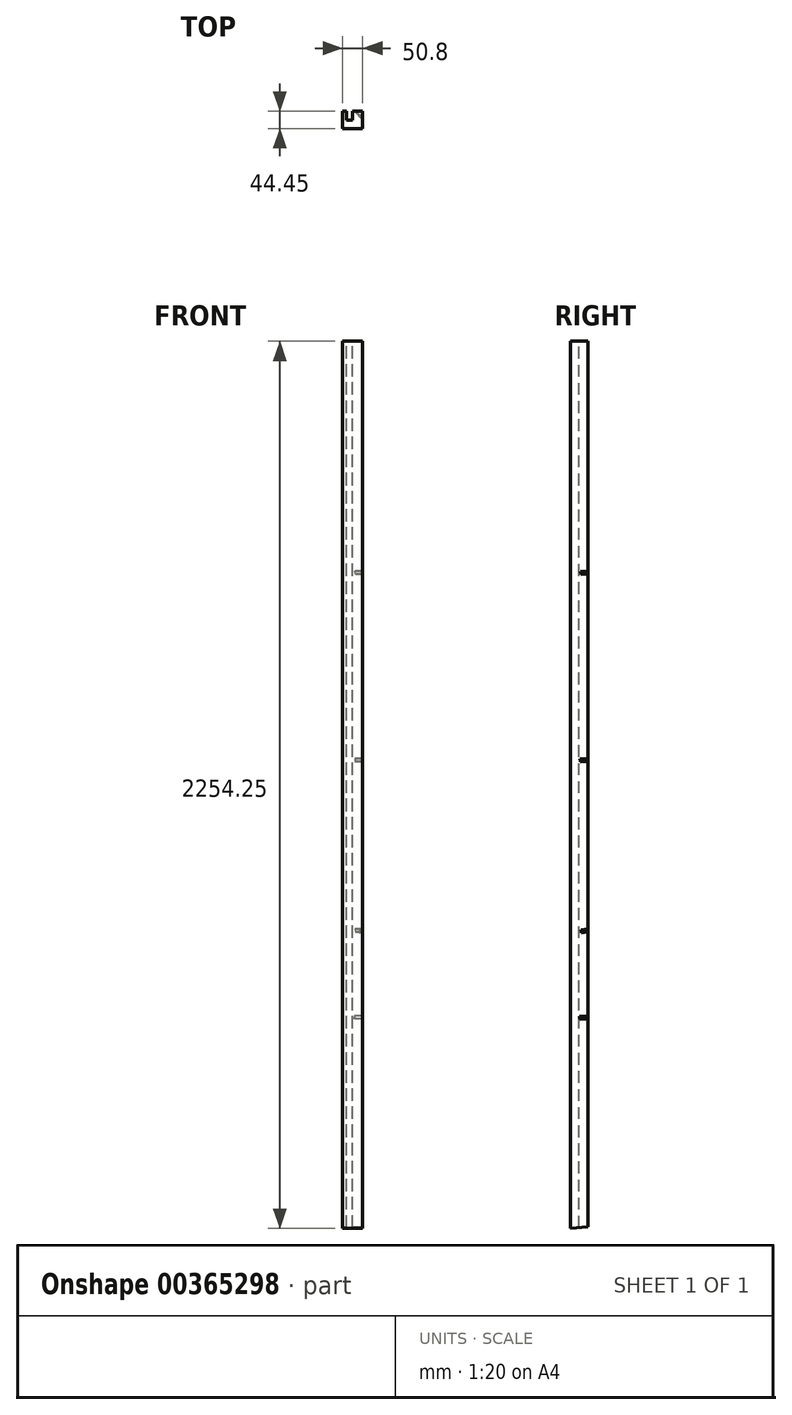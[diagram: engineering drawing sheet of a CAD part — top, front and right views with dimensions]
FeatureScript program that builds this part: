
annotation { "Feature Type Name" : "Feature", "Feature Type Description" : "" }
export const myFeature = defineFeature(function(context is Context, id is Id, definition is map)
    precondition{}
    {
        {
            var Q0;
            Q0=qCreatedBy(makeId("Top.planeOp"),FACE);
            var sketch = newSketch(context, id + "F0", { "sketchPlane" : qUnion([Q0])});
            skLineSegment(sketch, "E0.bottom", {"start": v(0, 0) * mm, "end": v(50.8, 0) * mm});
            skLineSegment(sketch, "E0.top", {"start": v(0, 44.45) * mm, "end": v(50.8, 44.45) * mm});
            skLineSegment(sketch, "E0.left", {"start": v(0, 0) * mm, "end": v(0, 44.45) * mm});
            skLineSegment(sketch, "E0.right", {"start": v(50.8, 0) * mm, "end": v(50.8, 44.45) * mm});
            skSolve(sketch);
        }
        {
            var Q0;
            Q0=makeQuery(id+"F0.imprint","IMPRINT",FACE,{"disambiguationData":[TD([[makeQuery(id+"F0.imprint","IMPRINT",EDGE,{"derivedFrom":sQuery(id+"F0.wireOp",EDGE,"E0.bottom")}),1.0]])]});
            extrude(context, id + "F1", {"entities" : qUnion([Q0]), "depth" : 2254.25 * mm});
        }
        {
            var Q0;
            Q0=makeQuery(id+"F1.opExtrude","CAP_FACE",FACE,{"disambiguationData":[OSD([sQuery(id+"F0.wireOp",EDGE,"E0.bottom"),sQuery(id+"F0.wireOp",EDGE,"E0.top"),sQuery(id+"F0.wireOp",EDGE,"E0.left"),sQuery(id+"F0.wireOp",EDGE,"E0.right")])],"isStart":false});
            var sketch = newSketch(context, id + "F2", { "sketchPlane" : qUnion([Q0])});
            skLineSegment(sketch, "E1.bottom", {"start": v(9.53, 44.45) * mm, "end": v(25.4, 44.45) * mm});
            skLineSegment(sketch, "E1.top", {"start": v(9.53, 22.23) * mm, "end": v(25.4, 22.23) * mm});
            skLineSegment(sketch, "E1.left", {"start": v(9.53, 44.45) * mm, "end": v(9.53, 22.23) * mm});
            skLineSegment(sketch, "E1.right", {"start": v(25.4, 44.45) * mm, "end": v(25.4, 22.23) * mm});
            skSolve(sketch);
        }
        {
            var Q0;
            Q0=makeQuery(id+"F2.imprint","IMPRINT",FACE,{"disambiguationData":[TD([[makeQuery(id+"F2.imprint","IMPRINT",EDGE,{"derivedFrom":sQuery(id+"F2.wireOp",EDGE,"E1.bottom")}),-1.0]])]});
            extrude(context, id + "F3", {"entities" : qUnion([Q0]), "operationType" : NewBodyOperationType.REMOVE, "oppositeDirection" : true, "depth" : 2260.6 * mm});
        }
        {
            var Q0;
            Q0=makeQuery(id+"F1.opExtrude","SWEPT_FACE",FACE,{"disambiguationData":[OSD([sQuery(id+"F0.wireOp",EDGE,"E0.right")])]});
            var sketch = newSketch(context, id + "F4", { "sketchPlane" : qUnion([Q0])});
            skLineSegment(sketch, "E2", {"start": v(0, 0) * mm, "end": v(44.45, 3.89) * mm});
            skLineSegment(sketch, "E3", {"start": v(44.45, 3.89) * mm, "end": v(44.45, 0) * mm});
            skLineSegment(sketch, "E4", {"start": v(44.45, 0) * mm, "end": v(0, 0) * mm});
            skSolve(sketch);
        }
        {
            var Q0;
            Q0=makeQuery(id+"F4.imprint","IMPRINT",FACE,{"disambiguationData":[TD([[makeQuery(id+"F4.imprint","IMPRINT",EDGE,{"derivedFrom":sQuery(id+"F4.wireOp",EDGE,"E2")}),-1.0]])]});
            extrude(context, id + "F5", {"entities" : qUnion([Q0]), "operationType" : NewBodyOperationType.REMOVE, "oppositeDirection" : true, "depth" : 76.2 * mm});
        }
        {
            var Q0;
            Q0=makeQuery(id+"F5.boolean.opBoolean","COPY",FACE,{"derivedFrom":makeQuery(id+"F5.opExtrude","SWEPT_FACE",FACE,{"disambiguationData":[OSD([sQuery(id+"F4.wireOp",EDGE,"E2")])]})});
            cPlane(context, id + "F6", {"entities" : qUnion([Q0]), "cplaneType" : CPlaneType.OFFSET, "offset" : 527.05 * mm, "oppositeDirection" : true, "width" : 152.4 * mm, "height" : 152.4 * mm});
        }
        {
            var Q0;
            Q0=makeQuery(id+"F5.boolean.opBoolean","COPY",FACE,{"derivedFrom":makeQuery(id+"F5.opExtrude","SWEPT_FACE",FACE,{"disambiguationData":[OSD([sQuery(id+"F4.wireOp",EDGE,"E2")])]})});
            cPlane(context, id + "F7", {"entities" : qUnion([Q0]), "cplaneType" : CPlaneType.OFFSET, "offset" : 746.12 * mm, "oppositeDirection" : true, "width" : 152.4 * mm, "height" : 152.4 * mm});
        }
        {
            var Q0;
            Q0=makeQuery(id+"F5.boolean.opBoolean","COPY",FACE,{"derivedFrom":makeQuery(id+"F5.opExtrude","SWEPT_FACE",FACE,{"disambiguationData":[OSD([sQuery(id+"F4.wireOp",EDGE,"E2")])]})});
            cPlane(context, id + "F8", {"entities" : qUnion([Q0]), "cplaneType" : CPlaneType.OFFSET, "offset" : 1177.92 * mm, "oppositeDirection" : true, "width" : 152.4 * mm, "height" : 152.4 * mm});
        }
        {
            var Q0;
            Q0=makeQuery(id+"F5.boolean.opBoolean","COPY",FACE,{"derivedFrom":makeQuery(id+"F5.opExtrude","SWEPT_FACE",FACE,{"disambiguationData":[OSD([sQuery(id+"F4.wireOp",EDGE,"E2")])]})});
            cPlane(context, id + "F9", {"entities" : qUnion([Q0]), "cplaneType" : CPlaneType.OFFSET, "offset" : 1660.52 * mm, "oppositeDirection" : true, "width" : 152.4 * mm, "height" : 152.4 * mm});
        }
        {
            var Q0;
            Q0=qCreatedBy(id+"F6.planeOp",FACE);
            var sketch = newSketch(context, id + "F10", { "sketchPlane" : qUnion([Q0])});
            skLineSegment(sketch, "E5", {"start": v(52.64, -68.17) * mm, "end": v(29.97, -90.85) * mm});
            skLineSegment(sketch, "E6", {"start": v(29.97, -90.85) * mm, "end": v(45.66, -106.54) * mm});
            skLineSegment(sketch, "E7", {"start": v(45.66, -106.54) * mm, "end": v(68.34, -83.87) * mm});
            skLineSegment(sketch, "E8", {"start": v(68.34, -83.87) * mm, "end": v(52.64, -68.17) * mm});
            skSolve(sketch);
        }
        {
            var Q0;
            Q0=makeQuery(id+"F10.imprint","IMPRINT",FACE,{"disambiguationData":[TD([[makeQuery(id+"F10.imprint","IMPRINT",EDGE,{"derivedFrom":sQuery(id+"F10.wireOp",EDGE,"E5")}),1.0]])]});
            extrude(context, id + "F11", {"entities" : qUnion([Q0]), "operationType" : NewBodyOperationType.REMOVE, "oppositeDirection" : true, "depth" : 7.62 * mm});
        }
        {
            var Q0;
            Q0=qCreatedBy(id+"F7.planeOp",FACE);
            var sketch = newSketch(context, id + "F12", { "sketchPlane" : qUnion([Q0])});
            skLineSegment(sketch, "E9", {"start": v(30.08, -111.42) * mm, "end": v(50.8, -93.16) * mm});
            skLineSegment(sketch, "E10", {"start": v(50.8, -93.16) * mm, "end": v(68.8, -113.6) * mm});
            skLineSegment(sketch, "E11", {"start": v(68.8, -113.6) * mm, "end": v(48.08, -131.84) * mm});
            skLineSegment(sketch, "E12", {"start": v(48.08, -131.84) * mm, "end": v(30.08, -111.42) * mm});
            skSolve(sketch);
        }
        {
            var Q0;
            Q0=makeQuery(id+"F12.imprint","IMPRINT",FACE,{"disambiguationData":[TD([[makeQuery(id+"F12.imprint","IMPRINT",EDGE,{"derivedFrom":sQuery(id+"F12.wireOp",EDGE,"E9")}),-1.0]])]});
            extrude(context, id + "F13", {"entities" : qUnion([Q0]), "operationType" : NewBodyOperationType.REMOVE, "oppositeDirection" : true, "depth" : 7.62 * mm});
        }
        {
            var Q0;
            Q0=qCreatedBy(id+"F8.planeOp",FACE);
            var sketch = newSketch(context, id + "F14", { "sketchPlane" : qUnion([Q0])});
            skLineSegment(sketch, "E13", {"start": v(31.75, -147.67) * mm, "end": v(50.8, -128.62) * mm});
            skLineSegment(sketch, "E14", {"start": v(50.8, -128.62) * mm, "end": v(65.5, -143.32) * mm});
            skLineSegment(sketch, "E15", {"start": v(65.5, -143.32) * mm, "end": v(46.44, -162.37) * mm});
            skLineSegment(sketch, "E16", {"start": v(46.44, -162.37) * mm, "end": v(31.75, -147.67) * mm});
            skLineSegment(sketch, "E17", {"start": v(31.75, -147.67) * mm, "end": v(50.8, -147.67) * mm, "construction": true});
            skLineSegment(sketch, "E18", {"start": v(50.8, -147.67) * mm, "end": v(50.8, -128.62) * mm, "construction": true});
            skSolve(sketch);
        }
        {
            var Q0;
            Q0=makeQuery(id+"F14.imprint","IMPRINT",FACE,{"disambiguationData":[TD([[makeQuery(id+"F14.imprint","IMPRINT",EDGE,{"derivedFrom":sQuery(id+"F14.wireOp",EDGE,"E13")}),-1.0]])]});
            extrude(context, id + "F15", {"entities" : qUnion([Q0]), "operationType" : NewBodyOperationType.REMOVE, "oppositeDirection" : true, "depth" : 7.62 * mm});
        }
        {
            var Q0;
            Q0=qCreatedBy(id+"F9.planeOp",FACE);
            var sketch = newSketch(context, id + "F16", { "sketchPlane" : qUnion([Q0])});
            skLineSegment(sketch, "E19", {"start": v(31.75, -189.9) * mm, "end": v(50.8, -170.85) * mm});
            skLineSegment(sketch, "E20", {"start": v(50.8, -170.85) * mm, "end": v(50.8, -189.9) * mm, "construction": true});
            skLineSegment(sketch, "E21", {"start": v(50.8, -189.9) * mm, "end": v(31.75, -189.9) * mm, "construction": true});
            skLineSegment(sketch, "E22", {"start": v(31.75, -189.9) * mm, "end": v(46.57, -204.71) * mm});
            skLineSegment(sketch, "E23", {"start": v(46.57, -204.71) * mm, "end": v(65.62, -185.66) * mm});
            skLineSegment(sketch, "E24", {"start": v(65.62, -185.66) * mm, "end": v(50.8, -170.85) * mm});
            skSolve(sketch);
        }
        {
            var Q0;
            Q0=makeQuery(id+"F16.imprint","IMPRINT",FACE,{"disambiguationData":[TD([[makeQuery(id+"F16.imprint","IMPRINT",EDGE,{"derivedFrom":sQuery(id+"F16.wireOp",EDGE,"E19")}),-1.0]])]});
            extrude(context, id + "F17", {"entities" : qUnion([Q0]), "operationType" : NewBodyOperationType.REMOVE, "depth" : 7.62 * mm});
        }
    });
